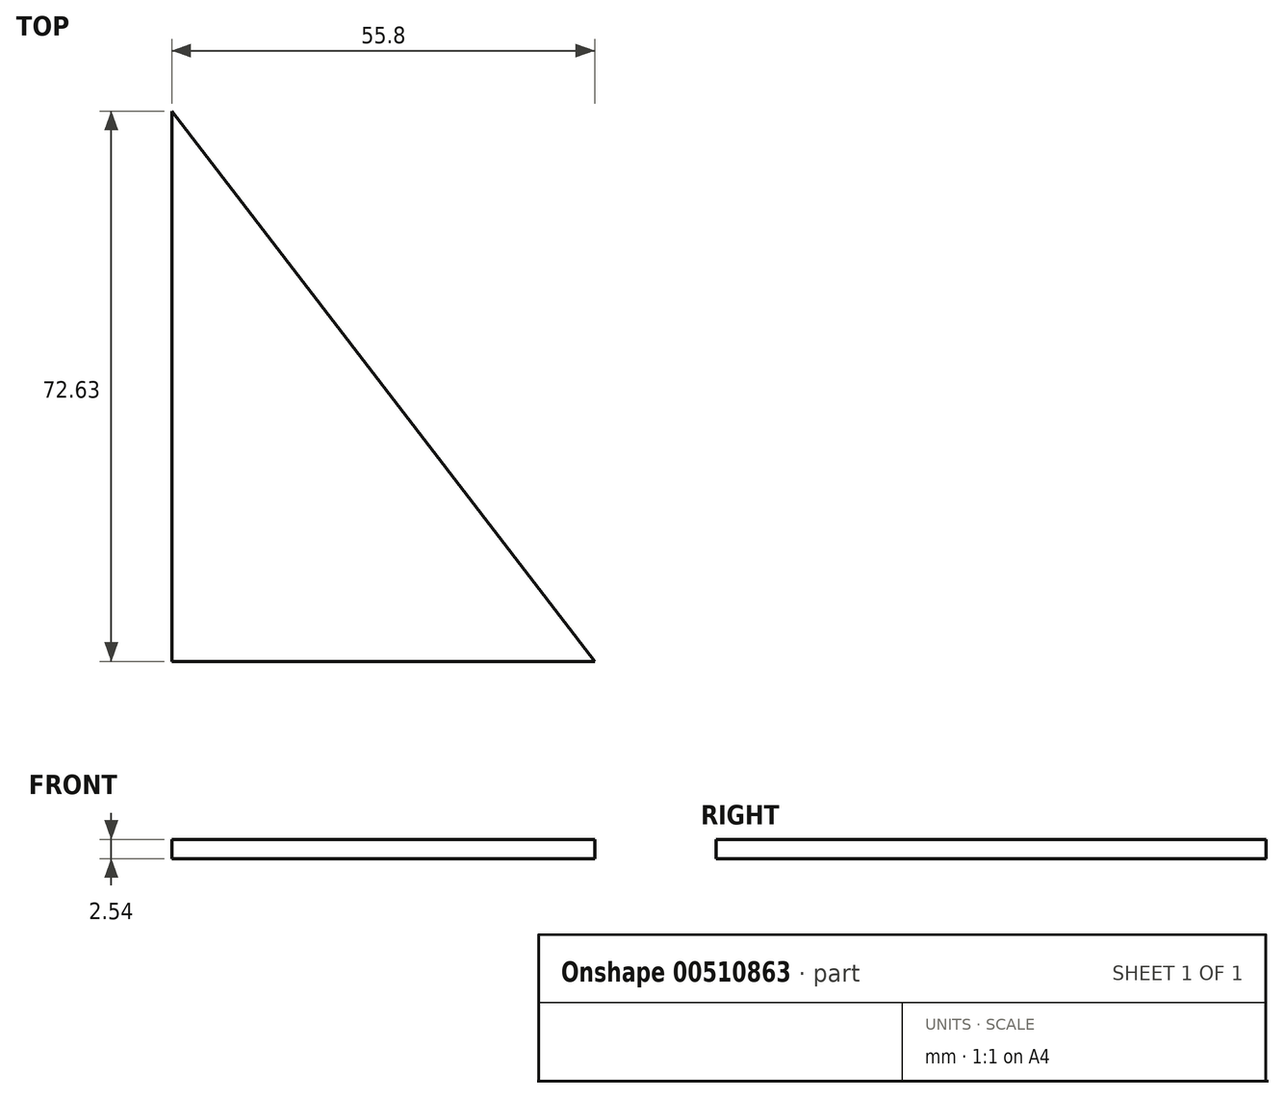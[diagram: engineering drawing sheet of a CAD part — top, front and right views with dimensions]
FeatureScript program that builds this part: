
annotation { "Feature Type Name" : "Feature", "Feature Type Description" : "" }
export const myFeature = defineFeature(function(context is Context, id is Id, definition is map)
    precondition{}
    {
        {
            var Q0;
            Q0=qCreatedBy(makeId("Top.planeOp"),FACE);
            var sketch = newSketch(context, id + "F0", { "sketchPlane" : qUnion([Q0])});
            skLineSegment(sketch, "E0", {"start": v(0, 0) * mm, "end": v(-55.8, 72.63) * mm});
            skLineSegment(sketch, "E1", {"start": v(-55.8, 72.63) * mm, "end": v(-55.8, 0) * mm});
            skLineSegment(sketch, "E2", {"start": v(-55.8, 0) * mm, "end": v(0, 0) * mm});
            skSolve(sketch);
        }
        {
            var Q0;
            Q0=makeQuery(id+"F0.imprint","IMPRINT",FACE,{"disambiguationData":[TD([[makeQuery(id+"F0.imprint","IMPRINT",EDGE,{"derivedFrom":sQuery(id+"F0.wireOp",EDGE,"E0")}),1.0]])]});
            extrude(context, id + "F1", {"entities" : qUnion([Q0]), "depth" : 2.54 * mm});
        }
    });
